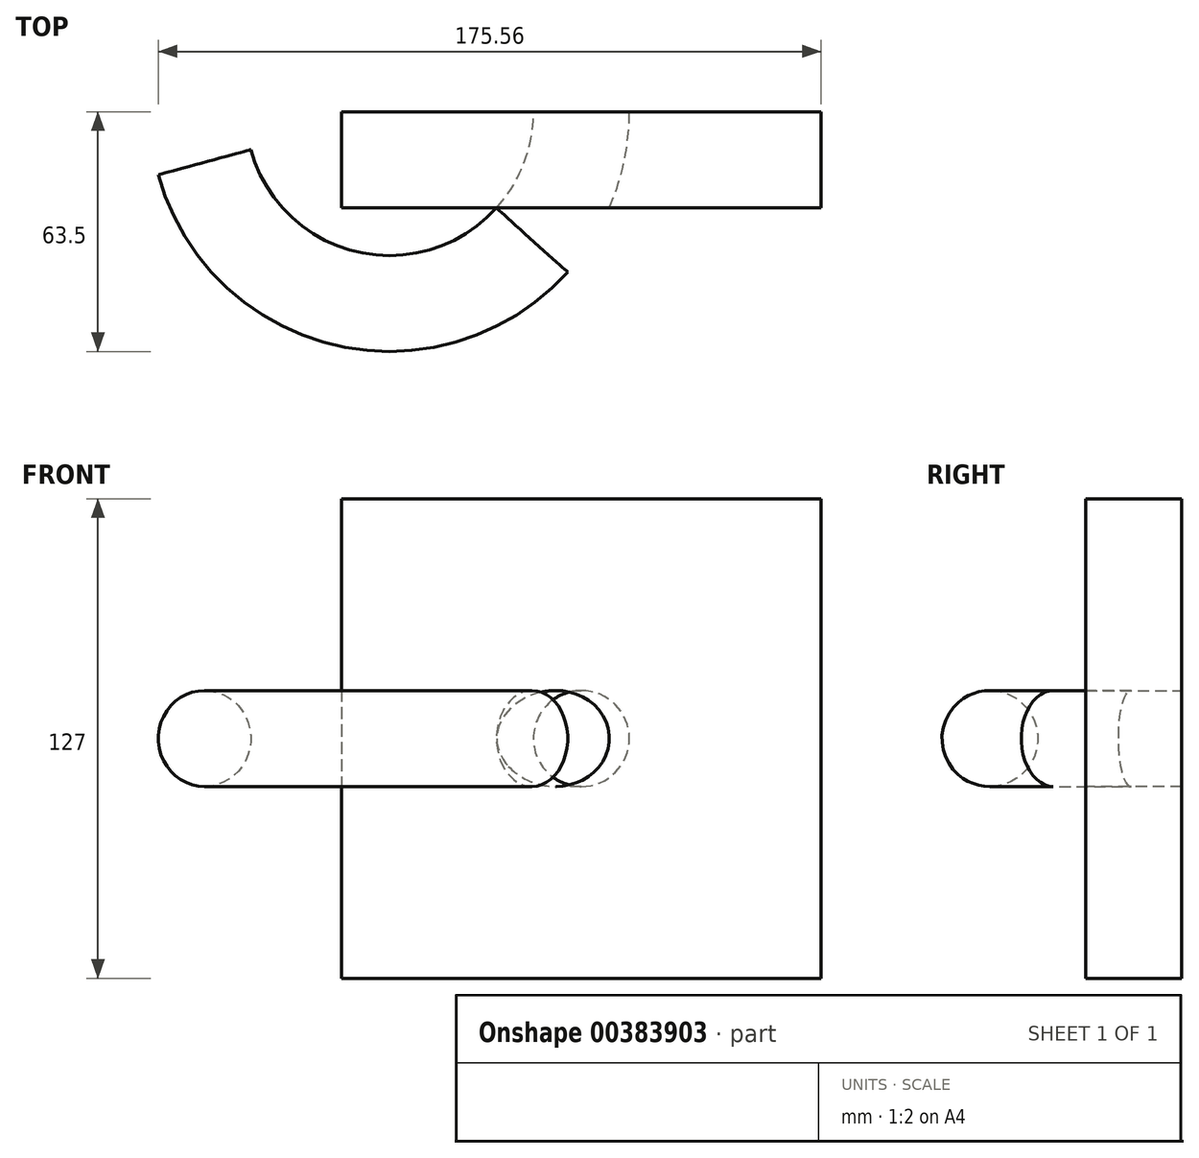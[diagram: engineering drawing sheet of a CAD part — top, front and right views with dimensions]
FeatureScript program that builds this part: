
annotation { "Feature Type Name" : "Feature", "Feature Type Description" : "" }
export const myFeature = defineFeature(function(context is Context, id is Id, definition is map)
    precondition{}
    {
        {
            var Q0;
            Q0=qCreatedBy(makeId("Front.planeOp"),FACE);
            var sketch = newSketch(context, id + "F0", { "sketchPlane" : qUnion([Q0])});
            skCircle(sketch, "E0", {"center": v(0, 0) * mm, "radius": 12.7 * mm});
            skSolve(sketch);
        }
        {
            var Q0;
            Q0=qCreatedBy(makeId("Front.planeOp"),FACE);
            var sketch = newSketch(context, id + "F1", { "sketchPlane" : qUnion([Q0])});
            skLineSegment(sketch, "E1.bottom", {"start": v(-63.5, 63.5) * mm, "end": v(63.5, 63.5) * mm});
            skLineSegment(sketch, "E1.top", {"start": v(-63.5, -63.5) * mm, "end": v(63.5, -63.5) * mm});
            skLineSegment(sketch, "E1.left", {"start": v(-63.5, 63.5) * mm, "end": v(-63.5, -63.5) * mm});
            skLineSegment(sketch, "E1.right", {"start": v(63.5, 63.5) * mm, "end": v(63.5, -63.5) * mm});
            skPoint(sketch, "E1.middle", {"position": v(0, 0) * mm});
            skSolve(sketch);
        }
        {
            var Q0;
            Q0=makeQuery(id+"F1.imprint","IMPRINT",FACE,{"disambiguationData":[TD([[makeQuery(id+"F1.imprint","IMPRINT",EDGE,{"derivedFrom":sQuery(id+"F1.wireOp",EDGE,"E1.bottom")}),-1.0]])]});
            extrude(context, id + "F2", {"entities" : qUnion([Q0]), "depth" : 25.4 * mm});
        }
        {
            var Q0;
            Q0=qCreatedBy(makeId("Top.planeOp"),FACE);
            var sketch = newSketch(context, id + "F3", { "sketchPlane" : qUnion([Q0])});
            skArc(sketch, "E2", {"start": v(-99.8, -13.38) * mm, "mid": v(-44.05, -50.35) * mm, "end": v(0, 0) * mm});
            skSolve(sketch);
        }
        {
            var Q0;
            Q0=makeQuery(id+"F0.imprint","IMPRINT",FACE,{"disambiguationData":[TD([[makeQuery(id+"F0.imprint","IMPRINT",EDGE,{"derivedFrom":sQuery(id+"F0.wireOp",EDGE,"E0")}),1.0]])]});
            var Q1;
            Q1=sQuery(id+"F3.wireOp",EDGE,"E2");
            sweep(context, id + "F4", {"profiles" : qUnion([Q0]), "path" : qUnion([Q1])});
        }
        {
            var Q0;
            Q0=qCreatedBy(makeId("Top.planeOp"),FACE);
            var sketch = newSketch(context, id + "F5", { "sketchPlane" : qUnion([Q0])});
            skArc(sketch, "E3", {"start": v(-13.06, -34) * mm, "mid": v(-3.38, -18.21) * mm, "end": v(0, 0) * mm});
            skSolve(sketch);
        }
        {
            var Q0;
            Q0=makeQuery(id+"F0.imprint","IMPRINT",FACE,{"disambiguationData":[TD([[makeQuery(id+"F0.imprint","IMPRINT",EDGE,{"derivedFrom":sQuery(id+"F0.wireOp",EDGE,"E0")}),1.0]])]});
            var Q1;
            Q1=sQuery(id+"F5.wireOp",EDGE,"E3");
            sweep(context, id + "F6", {"operationType" : NewBodyOperationType.REMOVE, "profiles" : qUnion([Q0]), "path" : qUnion([Q1])});
        }
    });
